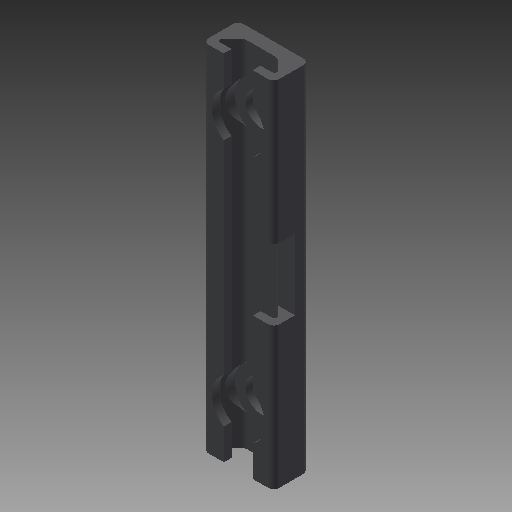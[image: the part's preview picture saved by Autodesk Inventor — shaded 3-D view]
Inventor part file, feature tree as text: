
AUTODESK INVENTOR PART (.ipt)
format: ipt  version: 2018 (Build 220112000, 112)  size: 178,688 bytes
history: native  units: mm
features: other x21, extrude x6, sketch x6
ambient origin geometry x8: Origin, YZ Plane, XZ Plane, XY Plane, X Axis, Y Axis, Z Axis, Center Point
bodies: Solid1 (feature_tree)
feature tree (33):
  extrude  "Extrusion1"  Depth=15.0mm TaperAngle=0.0deg
  extrude  "Extrusion2"  Depth=10.0mm TaperAngle=0.0deg
  extrude  "Extrusion3"  Depth=10.0mm TaperAngle=0.0deg
  extrude  "Extrusion4"  [1 undecoded]
  extrude  "Extrusion5"  [1 undecoded]
  extrude  "Extrusion6"  [1 undecoded]
  other  "side_1_XY"
  other  "side_1_YZ"
  other  "side_1_ZX"
  other  "side_1_X"
  other  "side_1_Y"
  other  "side_1_Z"
  other  "side_1_Center"
  other  "side_6a_XY"
  other  "side_6a_YZ"
  other  "side_6a_ZX"
  other  "side_6a_X"
  other  "side_6a_Y"
  other  "side_6a_Z"
  other  "side_6a_Center"
  other  "side_6b_XY"
  other  "side_6b_YZ"
  other  "side_6b_ZX"
  other  "side_6b_X"
  other  "side_6b_Y"
  other  "side_6b_Z"
  other  "side_6b_Center"
  sketch  "Skizze_1"  dims[d0=100.0mm d1=0.0mm d2=15.0mm d3=0.0mm]
  sketch  "Skizze_2"  dims[d8=10.0mm d9=0.0mm d10=10.0mm d11=0.0mm]
  sketch  "Skizze_3_ALT_Drilling_1"  dims[d4=10.0mm d5=0.0mm d6=10.0mm d7=0.0mm]
  sketch  "Skizze_4_ALT_Drilling_2"  dims[d12=0.0mm d13=0.0mm]
  sketch  "Skizze_5_ALT_Drilling_3"
  sketch  "Skizze_6_ALT_Drilling_4"
note: 3 required parameter values undecoded (feature->parameter linkage not recoverable at this tier; creation-order binding heuristic only, values carry confidence <= 0.55)
